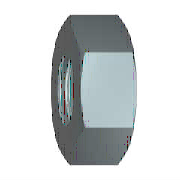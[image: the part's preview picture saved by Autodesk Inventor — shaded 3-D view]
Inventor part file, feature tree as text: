
AUTODESK INVENTOR PART (.ipt)
format: ipt  version: 2016 (Build 200138000, 138)  size: 160,768 bytes
history: native  units: mm (DEFAULTED — no unit token found)
features: sketch x3, chamfer x1, hole x1, other x1, plane x1
ambient origin geometry x7: Origin, YZ Plane, XZ Plane, X Axis, Y Axis, Z Axis, Center Point
bodies: Solid1 (feature_tree), Body (feature_tree)
feature tree (7):
  chamfer  "Chamfer1"  Angle=30.0deg  [1 undecoded]
  hole  "Thread"  [1 undecoded]
  other  "Work Axis1"
  plane  "Work Plane1"
  sketch  "Sketch1"  dims[d0=15.011107mm]
  sketch  "Sketch2"  dims[d1=6.5mm]
  sketch  "Sketch3"  dims[d2=0.0mm d3=30.0deg d4=30.0deg d5=11.5mm d6=11.5mm d7=90.0deg d25=6.647mm d26=6.0mm d27=4.0mm d28=2.0mm d29=14.3117mm d30=8.0mm d31=20.594885mm d8=0.676582mm d9=30.0deg d10=0.676582mm d11=30.0deg d13=0.0mm d14=0.0mm d39=0.0mm d40=0.676582mm d41=0.676582mm d42=0.0mm]
note: 2 required parameter values undecoded (feature->parameter linkage not recoverable at this tier; creation-order binding heuristic only, values carry confidence <= 0.55)
